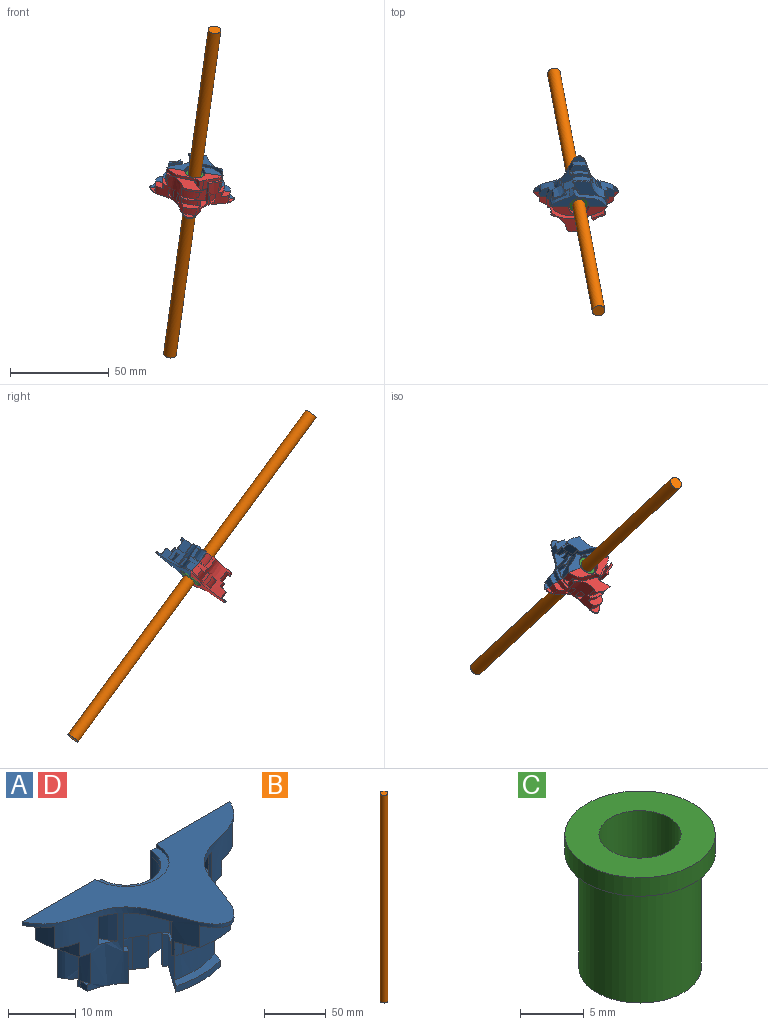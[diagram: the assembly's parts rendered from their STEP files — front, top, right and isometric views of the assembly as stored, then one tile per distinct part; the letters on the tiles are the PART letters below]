
ASSEMBLY  parts=4 mates=3
PART A: 74 faces, bbox 43.6x22.2x13.9 mm
  f0: extruded ~21.81x21.81mm, area 131.5mm2, adj f5,f6,f9,f11,f12,f14,f18,f23
  f1: cylinder r=11.8mm len=8.74mm, axis (0,0,1), area 46.6mm2, adj f7,f11,f23,f67
  f2: cylinder r=13.3mm len=8.08mm, axis (0,0,1), area 41.5mm2, adj f7,f11,f23,f67
  f3: cylinder r=14.27mm len=9.09mm, axis (0,0,1), area 50.1mm2, adj f8,f11,f34,f51,f67,f72
  f4: cylinder r=15.76mm len=8.18mm, axis (0,0,1), area 21.8mm2, adj f6,f8,f11,f67
  f5: cylinder r=15.76mm len=2.64mm, axis (0,0,1), area 3.6mm2, adj f0,f6,f9,f68
  f6: plane 9.61x4.01mm, normal (0,0,-1), area 26.7mm2, adj f0,f4,f5,f11,f26,f67,f68
  f7: plane 9.5x4.05mm, normal (0,0,1), area 12.9mm2, adj f1,f2,f11,f67
  f8: plane 8.82x2.56mm, normal (0,0,-1), area 12.3mm2, adj f3,f4,f11,f67
  f9: plane 1.49x0.8mm, normal (0,0,-1), area 0.3mm2, adj f0,f5,f68
  f10: plane 11x7.86mm, normal (0,0,-1), area 16.6mm2, adj f16,f35,f55,f56,f69,f70
  f11: extruded ~21.81x21.81mm, area 201.8mm2, adj f0,f1,f2,f3,f4,f6,f7,f8
  f12: plane 1.95x0.78mm, normal (0,0,1), area 0.4mm2, adj f0,f16,f35,f65,f66
  f13: plane 18.67x12.26mm, normal (0,0,-1), area 74.2mm2, adj f11,f17,f24,f51,f57,f63,f64
  f14: plane 6.79x4.89mm, normal (0,0,-1), area 7.2mm2, adj f0,f16,f53,f65,f66
  f15: plane 2.19x0.92mm, normal (0,0,1), area 0.7mm2, adj f11,f17,f22,f63,f64
  f16: extruded ~6.78x6mm, area 45.3mm2, adj f10,f12,f14,f35,f53,f66,f69,f71
  f17: extruded ~15.35x6mm, area 99.7mm2, adj f13,f15,f22,f54,f57,f63,f70,f72
  f18: plane 16.62x13.9mm, normal (0,1,0), area 145.5mm2, adj f0,f19,f20,f25,f28,f30,f35,f37
  f19: cylinder r=6.41mm len=12.82mm, axis (0,0,1), area 12mm2, adj f18,f47,f49,f58
  f20: plane 28.79x8.36mm, normal (0,0,-1), area 88.2mm2, adj f18,f47,f48,f52,f55,f56
  f21: plane 0.13x0.11mm, normal (0,0,1), area 0mm2, adj f22,f47,f52
  f22: cylinder r=14.27mm len=5.69mm, axis (0,0,1), area 14.4mm2, adj f11,f15,f17,f21,f36,f47,f52,f54
  f23: plane 15.84x9.96mm, normal (0,0,-1), area 53.6mm2, adj f0,f1,f2,f11,f67,f68,f69,f70
  f24: cylinder r=15.76mm len=9.37mm, axis (0,0,1), area 10.7mm2, adj f11,f13,f34,f51
  f25: plane 5.7x2.68mm, normal (0,0,-1), area 8.3mm2, adj f0,f18,f35,f37
  f26: cylinder r=19mm len=6.62mm, axis (0,0,1), area 26.6mm2, adj f0,f6,f11,f27
  f27: plane 6.86x3.22mm, normal (0,0,-1), area 12.3mm2, adj f0,f11,f26
  f28: cylinder r=11.8mm len=7.38mm, axis (0,0,1), area 39.9mm2, adj f0,f18,f30,f45
  f29: cylinder r=11.8mm len=7.38mm, axis (0,0,1), area 39.9mm2, adj f11,f31,f46,f47
  f30: plane 7.4x4.12mm, normal (0,0,-1), area 12mm2, adj f0,f18,f28,f32,f61,f62
  f31: plane 7.4x4.12mm, normal (0,0,-1), area 12mm2, adj f11,f29,f33,f47,f59,f60
  f32: cylinder r=13.3mm len=5mm, axis (0,0,1), area 6mm2, adj f0,f30,f45,f62
  f33: cylinder r=13.3mm len=5mm, axis (0,0,1), area 6mm2, adj f11,f31,f46,f60
  f34: plane 10.01x2.56mm, normal (0,0,1), area 14mm2, adj f3,f11,f24,f51
  f35: cylinder r=14.27mm len=5.69mm, axis (0,0,1), area 13.2mm2, adj f0,f10,f12,f16,f18,f25
  f36: plane 5.7x2.68mm, normal (0,0,-1), area 8.3mm2, adj f11,f22,f38,f47
  f37: cylinder r=15.76mm len=5.22mm, axis (0,0,1), area 14mm2, adj f0,f18,f25,f39
  f38: cylinder r=15.76mm len=5.22mm, axis (0,0,1), area 14mm2, adj f11,f36,f40,f47
  f39: plane 5.26x4.17mm, normal (0,0,-1), area 15mm2, adj f0,f18,f37,f41
  f40: plane 5.26x4.17mm, normal (0,0,-1), area 15mm2, adj f11,f38,f42,f47
  f41: cylinder r=19mm len=4mm, axis (0,0,1), area 15mm2, adj f0,f18,f39,f43
  f42: cylinder r=19mm len=4mm, axis (0,0,1), area 15mm2, adj f11,f40,f44,f47
  f43: plane 3.8x3.26mm, normal (0,0,-1), area 6.2mm2, adj f0,f18,f41
  f44: plane 3.8x3.26mm, normal (0,0,-1), area 6.2mm2, adj f11,f42,f47
  f45: plane 7.4x4.12mm, normal (0,0,1), area 12mm2, adj f0,f18,f28,f32,f61,f62
  f46: plane 7.4x4.12mm, normal (0,0,1), area 12mm2, adj f11,f29,f33,f47,f59,f60
  f47: plane 16.62x13.92mm, normal (0,1,0), area 145.8mm2, adj f11,f19,f20,f21,f22,f29,f31,f36
  f48: cylinder r=5.2mm len=12.18mm, axis (0,0,1), area 199mm2, adj f18,f20,f47,f50
  f49: plane 12.82x6.41mm, normal (0,0,1), area 22.3mm2, adj f18,f19,f47,f50
  f50: cone r=5.2mm half-angle=0.8deg, axis (0,0,-1), area 18.3mm2, adj f18,f47,f48,f49
  f51: plane 5.79x5.61mm, normal (-0.81,0.58,0), area 32.6mm2, adj f3,f13,f24,f34,f57,f72
  f52: extruded ~17.35x7.76mm, area 119mm2, adj f20,f21,f22,f47,f54,f56,f70,f73
  f53: plane 5.79x1.15mm, normal (0.81,-0.58,0), area 8.2mm2, adj f0,f14,f16,f71
  f54: plane 17.48x8.67mm, normal (0,0,-1), area 36.2mm2, adj f17,f22,f52,f70
  f55: extruded ~9.29x6.33mm, area 68.8mm2, adj f10,f18,f20,f56
  f56: plane 6x2.02mm, normal (-0.58,-0.81,0), area 14.7mm2, adj f10,f20,f52,f55,f70,f73
  f57: plane 5.79x0.76mm, normal (-0.58,-0.81,0), area 5.4mm2, adj f13,f17,f51,f72
  f58: plane 43.61x21.81mm, normal (0,0,1), area 331.4mm2, adj f0,f11,f18,f19,f47
  f59: plane 5x5mm, normal (-1,0,0), area 25mm2, adj f31,f46,f47,f60
  f60: plane 5x0.98mm, normal (0,1,0), area 4.9mm2, adj f31,f33,f46,f59
  f61: plane 5x5mm, normal (1,0,0), area 25mm2, adj f18,f30,f45,f62
  f62: plane 5x0.98mm, normal (0,1,0), area 4.9mm2, adj f30,f32,f45,f61
  f63: plane 1.13x0.33mm, normal (0.92,-0.4,0), area 0.4mm2, adj f13,f15,f17,f64
  f64: plane 1.65x1.13mm, normal (1,0,0), area 1.9mm2, adj f11,f13,f15,f63
  f65: plane 1.46x1.13mm, normal (-1,0,0), area 1.6mm2, adj f0,f12,f14,f66
  f66: plane 1.13x0.33mm, normal (-0.86,-0.5,0), area 0.4mm2, adj f12,f14,f16,f65
  f67: plane 7x6.16mm, normal (-0.88,0.47,0), area 39.7mm2, adj f1,f2,f3,f4,f6,f7,f8,f23
  f68: plane 6.17x1.54mm, normal (0.47,0.88,0), area 10.6mm2, adj f0,f5,f6,f9,f23,f67
  f69: plane 7x2.51mm, normal (0.88,-0.47,0), area 19.6mm2, adj f0,f10,f16,f23,f70,f71
  f70: plane 7.04x7mm, normal (-0.47,-0.88,0), area 54.7mm2, adj f10,f17,f23,f52,f54,f56,f67,f69
  f71: plane 1.6x1.4mm, normal (0,0,1), area 1.1mm2, adj f0,f16,f53,f69
  f72: plane 5.36x3.59mm, normal (0,0,1), area 3.9mm2, adj f3,f17,f51,f57,f67,f70
  f73: plane 0.48x0.31mm, normal (0,0,1), area 0mm2, adj f52,f56,f70
PART B: 3 faces, bbox 6.4x6.4x205 mm
  f0: cylinder r=3.21mm len=205mm, axis (0,0,-1), area 4134.7mm2, adj f1,f2
  f1: plane 6.42x6.42mm, normal (0,0,1), area 32.4mm2, adj f0
  f2: plane 6.42x6.42mm, normal (0,0,-1), area 32.4mm2, adj f0
PART C: 6 faces, bbox 11.8x11.8x12.8 mm
  f0: cylinder r=4.79mm len=11mm, axis (0,0,-1), area 330.7mm2, adj f3,f5
  f1: cylinder r=3.21mm len=12.76mm, axis (0,0,-1), area 257.4mm2, adj f2,f3
  f2: plane 11.76x11.76mm, normal (0,0,1), area 76.2mm2, adj f1,f4
  f3: plane 9.57x9.57mm, normal (0,0,-1), area 39.6mm2, adj f0,f1
  f4: cylinder r=5.88mm len=11.76mm, axis (0,0,-1), area 65mm2, adj f2,f5
  f5: plane 11.76x11.76mm, normal (0,0,-1), area 36.7mm2, adj f0,f4
PART D: same geometry as A
PLACE A rot(axis=(-1,0.02,0.07),144.1deg) t=(42.32,-262.67,422.65)mm
PLACE B rot(axis=(-1,0.02,0.07),144.1deg) t=(30.45,-137.35,336.12)mm
PLACE C rot(axis=(-0.71,-0.68,-0.18),149.4deg) t=(31.39,-142.35,342.93)mm
PLACE D rot(axis=(-0.02,-0.95,-0.31),172.5deg) t=(50.4,-181.78,480.89)mm
MATE revolute C.f0 <-> B.f0  axis (0.11,-0.59,0.8) through (19.14,-77.08,253.99)mm
MATE fastened D.f18 <-> A.f47  axis (0.08,0.81,0.58) through (30.19,-84.56,262.86)mm
MATE revolute C.f0 <-> D.f1  axis (0.11,-0.59,0.8) through (19.04,-76.56,253.28)mm
